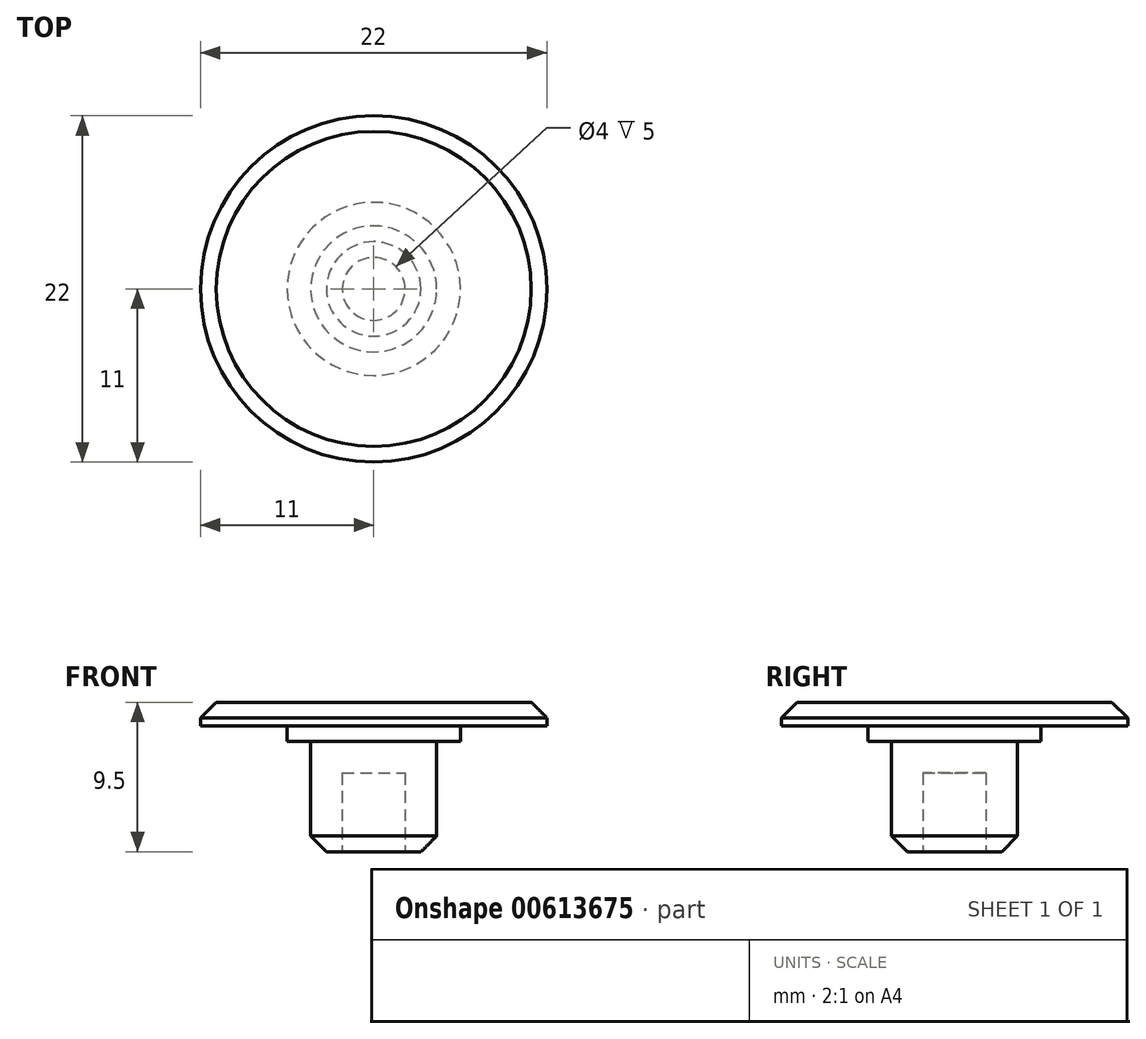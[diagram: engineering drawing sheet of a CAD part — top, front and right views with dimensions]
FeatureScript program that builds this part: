
annotation { "Feature Type Name" : "Feature", "Feature Type Description" : "" }
export const myFeature = defineFeature(function(context is Context, id is Id, definition is map)
    precondition{}
    {
        {
            var Q0;
            Q0=qCreatedBy(makeId("Top.planeOp"),FACE);
            var sketch = newSketch(context, id + "F0", { "sketchPlane" : qUnion([Q0])});
            skCircle(sketch, "E0", {"center": v(0, 0) * mm, "radius": 4 * mm});
            skSolve(sketch);
        }
        {
            var Q0;
            Q0=makeQuery(id+"F0.imprint","IMPRINT",FACE,{"disambiguationData":[TD([[makeQuery(id+"F0.imprint","IMPRINT",EDGE,{"derivedFrom":sQuery(id+"F0.wireOp",EDGE,"E0")}),1.0]])]});
            extrude(context, id + "F1", {"entities" : qUnion([Q0]), "depth" : 7 * mm, "offsetDistance" : 25 * mm});
        }
        {
            var Q0;
            Q0=makeQuery(id+"F1.opExtrude","CAP_FACE",FACE,{"disambiguationData":[OSD([sQuery(id+"F0.wireOp",EDGE,"E0")])],"isStart":false});
            var sketch = newSketch(context, id + "F2", { "sketchPlane" : qUnion([Q0])});
            skCircle(sketch, "E1", {"center": v(0, 0) * mm, "radius": 5.5 * mm});
            skSolve(sketch);
        }
        {
            var Q0;
            Q0=makeQuery(id+"F2.imprint","IMPRINT",FACE,{"disambiguationData":[TD([[makeQuery(id+"F2.imprint","IMPRINT",EDGE,{"derivedFrom":sQuery(id+"F2.wireOp",EDGE,"E1")}),1.0]])]});
            var Q1;
            Q1=makeQuery(id+"F2.imprint","IMPRINT",FACE,{"disambiguationData":[TD([[makeQuery(id+"F2.imprint","IMPRINT",EDGE,{"derivedFrom":makeQuery(id+"F1.opExtrude","CAP_EDGE",EDGE,{"disambiguationData":[OSD([sQuery(id+"F0.wireOp",EDGE,"E0")])],"isStart":false})}),1.0]])]});
            extrude(context, id + "F3", {"entities" : qUnion([Q0, Q1]), "operationType" : NewBodyOperationType.ADD, "depth" : 1 * mm, "offsetDistance" : 25 * mm});
        }
        {
            var Q0;
            Q0=makeQuery(id+"F3.opExtrude","CAP_FACE",FACE,{"disambiguationData":[OSD([sQuery(id+"F2.wireOp",EDGE,"E1")])],"isStart":false});
            var sketch = newSketch(context, id + "F4", { "sketchPlane" : qUnion([Q0])});
            skCircle(sketch, "E2", {"center": v(0, 0) * mm, "radius": 11 * mm});
            skSolve(sketch);
        }
        {
            var Q0;
            Q0 = qSketchRegion(id + "F4", true);
            extrude(context, id + "F5", {"entities" : qUnion([Q0]), "operationType" : NewBodyOperationType.ADD, "depth" : 1.5 * mm, "offsetDistance" : 25 * mm});
        }
        {
            var Q0;
            Q0=makeQuery(id+"F1.opExtrude","CAP_FACE",FACE,{"disambiguationData":[OSD([sQuery(id+"F0.wireOp",EDGE,"E0")])],"isStart":true});
            var sketch = newSketch(context, id + "F6", { "sketchPlane" : qUnion([Q0])});
            skCircle(sketch, "E3", {"center": v(0, 0) * mm, "radius": 2 * mm});
            skSolve(sketch);
        }
        {
            var Q0;
            Q0 = qSketchRegion(id + "F6", true);
            extrude(context, id + "F7", {"entities" : qUnion([Q0]), "operationType" : NewBodyOperationType.REMOVE, "oppositeDirection" : true, "depth" : 5 * mm, "offsetDistance" : 25 * mm});
        }
        {
            var Q0;
            Q0=makeQuery(id+"F1.opExtrude","CAP_EDGE",EDGE,{"disambiguationData":[OSD([sQuery(id+"F0.wireOp",EDGE,"E0")])],"isStart":true});
            chamfer(context, id + "F8", {"entities" : qUnion([Q0]), "width" : 1 * mm, "tangentPropagation" : true});
        }
        {
            var Q0;
            Q0=makeQuery(id+"F5.opExtrude","CAP_EDGE",EDGE,{"disambiguationData":[OSD([sQuery(id+"F4.wireOp",EDGE,"E2")])],"isStart":false});
            chamfer(context, id + "F9", {"entities" : qUnion([Q0]), "width" : 1 * mm, "tangentPropagation" : true});
        }
    });
